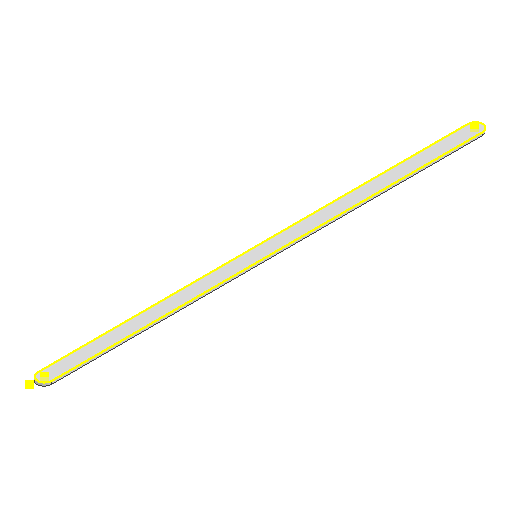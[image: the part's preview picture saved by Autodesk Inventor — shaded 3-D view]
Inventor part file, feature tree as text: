
AUTODESK INVENTOR PART (.ipt)
format: ipt  version: 2022 (Build 260153000, 153)  size: 110,592 bytes
history: native  units: mm
features: extrude x3, sketch x3, projected_geometry x2
ambient origin geometry x8: Origin, YZ Plane, XZ Plane, XY Plane, X Axis, Y Axis, Z Axis, Center Point
bodies: Solid1 (feature_tree)
feature tree (8):
  extrude  "Extrusion1"  Depth=8.0mm
  sketch  "Sketch2"  dims[d2=3.0mm d3=3.0mm]
  extrude  "Extrusion2"  Depth=3.0mm
  extrude  "Extrusion3"  Depth=8.0mm
  sketch  "Sketch3"  dims[d4=4.5mm d5=0.0mm d6=8.0mm d7=16.0mm d8=8.0mm d9=2.0mm d10=0.0mm d11=100.0mm d12=0.0mm]
  sketch  "Sketch1"  dims[d0=263.803mm d1=8.0mm]
  projected_geometry  "Projected Loop1"
  projected_geometry  "Projected Loop2"
